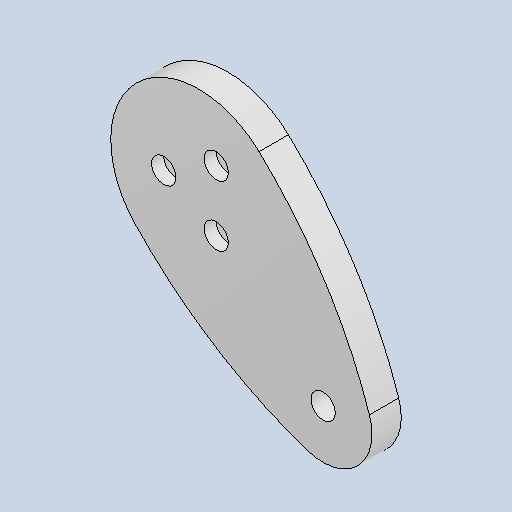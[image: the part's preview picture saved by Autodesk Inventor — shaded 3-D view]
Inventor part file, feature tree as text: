
AUTODESK INVENTOR PART (.ipt)
format: ipt  version: 2023 (Build 270158000, 158)  size: 153,088 bytes
history: native  units: mm
features: other x4, sketch x2
ambient origin geometry x8: Origin, YZ Plane, XZ Plane, XY Plane, X Axis, Y Axis, Z Axis, Center Point
bodies: Body1 (feature_tree)
feature tree (6):
  other  "クランク_前.ipt"
  other  "Solid2::クランク_前.ipt"
  other  "TaggingFeature1"
  sketch  "Sketch2"  dims[d0=10.0mm]
  sketch  "Sketch3"
  other  "sesaku"
